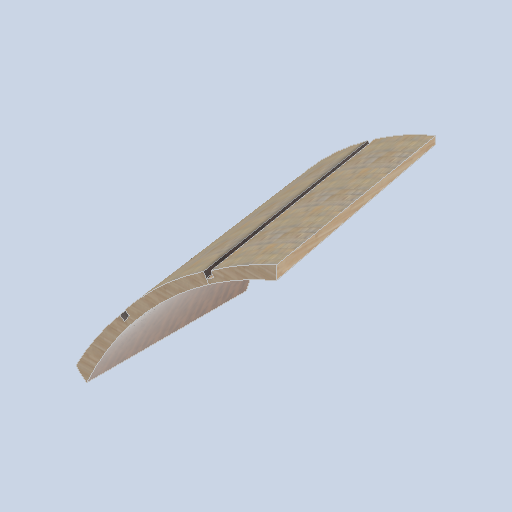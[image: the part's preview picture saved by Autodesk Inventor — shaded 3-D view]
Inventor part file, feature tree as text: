
AUTODESK INVENTOR PART (.ipt)
format: ipt  version: 2024.2 (Build 282272000, 272)  size: 268,800 bytes
history: native  units: in
note: dims shown in document units (in); Inventor stores cm internally (conversion verified against a paired STEP export)
features: sketch x7, other x3, plane x2
ambient origin geometry x8: Origin, YZ Plane, XZ Plane, XY Plane, X Axis, Y Axis, Z Axis, Center Point
bodies: Solid1 (feature_tree)
feature tree (12):
  other  "panel_block_01.ipt"
  other  "Solid1::panel_block_01.ipt"
  other  "TaggingFeature1"
  sketch  "Sketch3"  dims[d0=0.3937in]
  sketch  "Sketch8"
  sketch  "Sketch9"
  sketch  "Sketch10"
  sketch  "Sketch11"
  sketch  "Sketch14"
  sketch  "Sketch15"
  plane  "Work Plane1"
  plane  "Work Plane2"
